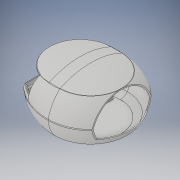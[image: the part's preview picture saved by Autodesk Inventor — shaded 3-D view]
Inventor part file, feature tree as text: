
AUTODESK INVENTOR PART (.ipt)
format: ipt  version: 2019 (Build 230136000, 136)  size: 2,665,472 bytes
history: native  units: mm
features: sketch x34, other x31, extrude x17, loft x12, pattern_linear x12, projected_geometry x12, fillet x10, mirror x5, revolve x3
ambient origin geometry x8: Origin, YZ Plane, XZ Plane, XY Plane, X Axis, Y Axis, Z Axis, Center Point
bodies: Body1 (feature_tree), Body2 (feature_tree)
feature tree (136):
  other  "голова"
  other  "Твердое тело1"
  sketch  "Эскиз1"
  extrude  "Выдавливание1"  Depth=42.3mm
  extrude  "Выдавливание2"  Depth=20.3mm
  extrude  "Выдавливание3"  Depth=40.0mm
  other  "РабПлоскость1"
  sketch  "Эскиз3"
  other  "РабПлоскость2"
  loft  "Лофт1"
  other  "РабПлоскость3"
  sketch  "Эскиз5"
  loft  "Лофт3"
  other  "РабПлоскость4"
  sketch  "Эскиз8"
  other  "РабПлоскость6"
  sketch  "Эскиз9"
  loft  "Лофт4"
  extrude  "Выдавливание4"  Depth=100.0mm
  mirror  "Зеркальное отражение1"
  loft  "Лофт5"
  loft  "Лофт6"
  loft  "Лофт7"
  sketch  "Эскиз11"
  extrude  "Выдавливание5"  Depth=20.0mm
  mirror  "Зеркальное отражение2"
  sketch  "Эскиз13"
  other  "РабПлоскость7"
  sketch  "Эскиз14"
  other  "РабПлоскость9"
  sketch  "Эскиз16"
  other  "РабПлоскость10"
  sketch  "Эскиз17"
  other  "РабПлоскость8"
  extrude  "Выдавливание6"  Depth=2.0mm TaperAngle=0.0deg
  loft  "Лофт8"
  mirror  "Зеркальное отражение3"
  other  "РабПлоскость11"
  revolve  "Вращение1"
  extrude  "Выдавливание7"  Depth=2.0mm
  loft  "Лофт9"
  loft  "Лофт10"
  other  "РабПлоскость12"
  sketch  "Эскиз20"
  sketch  "Эскиз21"
  sketch  "Эскиз22"
  loft  "Лофт11"
  loft  "Лофт12"
  mirror  "Зеркальное отражение4"
  other  "РабПлоскость13"
  loft  "Лофт13"
  extrude  "Выдавливание9"  Depth=50.0mm
  fillet  "Сопряжение1"  Radius=52.0mm
  fillet  "Сопряжение2"  Radius=2.0mm
  fillet  "Сопряжение3"  Radius=2.0mm
  fillet  "Сопряжение4"  Radius=46.0mm
  fillet  "Сопряжение5"  Radius=31.0mm
  fillet  "Сопряжение6"  Radius=30.0mm
  fillet  "Сопряжение7"  Radius=2.0mm
  extrude  "Выдавливание10"  Depth=2.0mm
  pattern_linear  "Прямоуг.массив1"  Spacing1=2.0mm  [1 undecoded]
  pattern_linear  "Прямоуг.массив2"  Spacing1=98.851581mm  [1 undecoded]
  pattern_linear  "Прямоуг.массив3"  Spacing1=40.790396mm  [1 undecoded]
  pattern_linear  "Прямоуг.массив4"  Spacing1=0.0mm  [1 undecoded]
  pattern_linear  "Прямоуг.массив5"  Spacing1=0.0mm  [1 undecoded]
  pattern_linear  "Прямоуг.массив6"  Spacing1=2.0mm  [1 undecoded]
  pattern_linear  "Прямоуг.массив7"  Spacing1=2.0mm  [1 undecoded]
  pattern_linear  "Прямоуг.массив8"  Spacing1=2.0mm  [1 undecoded]
  pattern_linear  "Прямоуг.массив9"  Spacing1=83.118457mm  [1 undecoded]
  pattern_linear  "Прямоуг.массив10"  Spacing1=1.99778mm  [1 undecoded]
  pattern_linear  "Прямоуг.массив11"  Spacing1=0.0mm  [1 undecoded]
  pattern_linear  "Прямоуг.массив12"  Spacing1=0.0mm  [1 undecoded]
  mirror  "Зеркальное отражение5"
  fillet  "Сопряжение8"  Radius=2.0mm
  fillet  "Сопряжение9"  Radius=2.0mm
  fillet  "Сопряжение10"  Radius=2.0mm
  extrude  "Выдавливание12"  Depth=53.0mm
  revolve  "Вращение2"
  extrude  "Выдавливание13"  Depth=2.0mm
  revolve  "Вращение3"
  other  "РабПлоскость14"
  sketch  "Эскиз35"
  extrude  "Выдавливание14"  TaperAngle=0.0deg  [1 undecoded]
  extrude  "Выдавливание15"  TaperAngle=0.0deg  [1 undecoded]
  other  "РабПлоскость15"
  extrude  "Выдавливание17"  TaperAngle=0.0deg  [1 undecoded]
  extrude  "Выдавливание20"  Depth=60.0mm TaperAngle=0.0deg
  sketch  "Эскиз47"
  extrude  "Выдавливание21"  TaperAngle=0.0deg  [1 undecoded]
  extrude  "Выдавливание22"  TaperAngle=0.0deg  [1 undecoded]
  sketch  "Эскиз2"
  sketch  "Эскиз4"
  projected_geometry  "Спроецированная петля1"
  other  "Ребра2"
  projected_geometry  "Спроецированная петля2"
  other  "Ребра3"
  other  "Ребра1"
  sketch  "Эскиз10"
  projected_geometry  "Спроецированная петля3"
  other  "Ребра4"
  other  "Ребра5"
  other  "Ребра6"
  other  "Ребра7"
  other  "Ребра8"
  other  "Ребра9"
  sketch  "Эскиз12"
  projected_geometry  "Спроецированная петля4"
  sketch  "Эскиз15"
  projected_geometry  "Спроецированная петля5"
  other  "Ребра10"
  sketch  "Эскиз18"
  sketch  "Эскиз19"
  projected_geometry  "Спроецированная петля6"
  other  "Ребра11"
  other  "Ребра12"
  other  "Ребра13"
  other  "Ребра14"
  projected_geometry  "Спроецированная петля7"
  projected_geometry  "Спроецированная петля8"
  other  "Ребра15"
  sketch  "Эскиз24"
  sketch  "Эскиз25"
  projected_geometry  "Спроецированная петля10"
  sketch  "Эскиз26"
  sketch  "Эскиз27"
  sketch  "Эскиз29"
  sketch  "Эскиз32"
  projected_geometry  "Спроецированная петля11"
  sketch  "Эскиз33"
  sketch  "Эскиз34"
  sketch  "Эскиз37"
  sketch  "Эскиз38"
  sketch  "Эскиз40"
  sketch  "Эскиз46"
  projected_geometry  "Спроецированная петля16"
  projected_geometry  "Спроецированная петля17"
note: 17 required parameter values undecoded (feature->parameter linkage not recoverable at this tier; creation-order binding heuristic only, values carry confidence <= 0.55)
